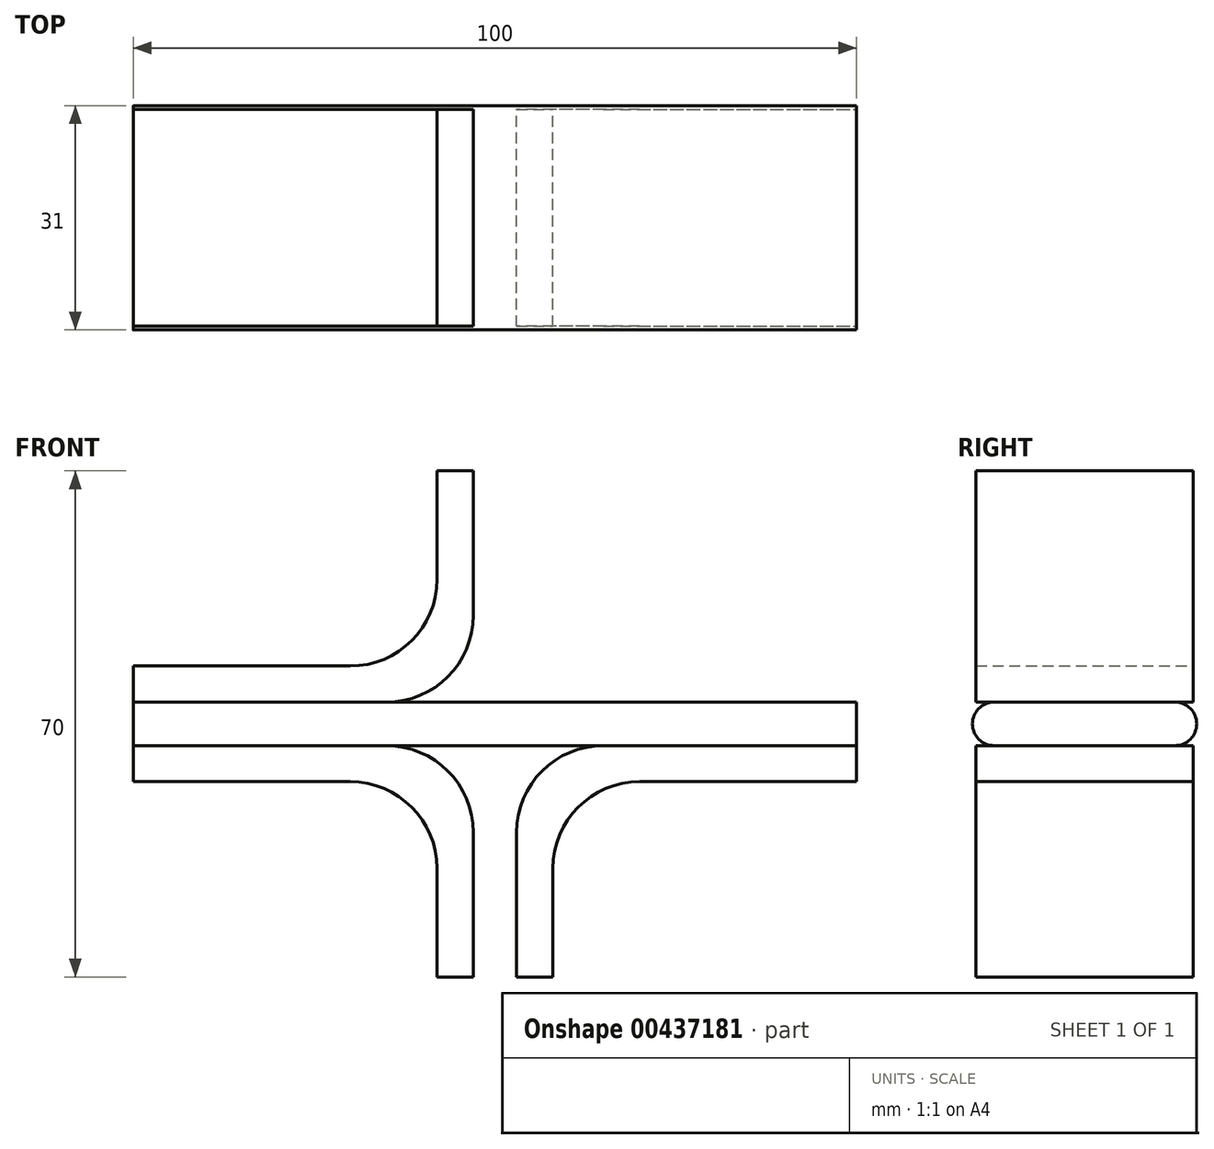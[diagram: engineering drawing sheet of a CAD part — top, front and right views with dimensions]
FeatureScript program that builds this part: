
annotation { "Feature Type Name" : "Feature", "Feature Type Description" : "" }
export const myFeature = defineFeature(function(context is Context, id is Id, definition is map)
    precondition{}
    {
        {
            var Q0;
            Q0=qCreatedBy(makeId("Right.planeOp"),FACE);
            var sketch = newSketch(context, id + "F0", { "sketchPlane" : qUnion([Q0])});
            skArc(sketch, "E0", {"start": v(-12.5, 3) * mm, "mid": v(-15.5, 0) * mm, "end": v(-12.5, -3) * mm});
            skArc(sketch, "E1", {"start": v(12.5, 3) * mm, "mid": v(15.5, 0) * mm, "end": v(12.5, -3) * mm});
            skLineSegment(sketch, "E2", {"start": v(-12.5, 3) * mm, "end": v(12.5, 3) * mm});
            skLineSegment(sketch, "E3", {"start": v(-12.5, -3) * mm, "end": v(12.5, -3) * mm});
            skSolve(sketch);
        }
        {
            var Q0;
            Q0=makeQuery(id+"F0.imprint","IMPRINT",FACE,{"disambiguationData":[TD([[makeQuery(id+"F0.imprint","IMPRINT",EDGE,{"derivedFrom":sQuery(id+"F0.wireOp",EDGE,"E0")}),1.0]])]});
            extrude(context, id + "F1", {"entities" : qUnion([Q0]), "endBound" : BoundingType.SYMMETRIC, "depth" : 100 * mm});
        }
        {
            var Q0;
            Q0=qCreatedBy(makeId("Front.planeOp"),FACE);
            var sketch = newSketch(context, id + "F2", { "sketchPlane" : qUnion([Q0])});
            skLineSegment(sketch, "E4", {"start": v(-50, 8) * mm, "end": v(-50, 3) * mm});
            skLineSegment(sketch, "E5", {"start": v(-50, 3) * mm, "end": v(-15, 3) * mm});
            skLineSegment(sketch, "E6", {"start": v(-3, 15) * mm, "end": v(-3, 35) * mm});
            skLineSegment(sketch, "E7", {"start": v(-3, 35) * mm, "end": v(-8, 35) * mm});
            skLineSegment(sketch, "E8", {"start": v(-8, 35) * mm, "end": v(-8, 20) * mm});
            skLineSegment(sketch, "E9", {"start": v(-20, 8) * mm, "end": v(-50, 8) * mm});
            skPoint(sketch, "E10.visualSharp", {"position": v(-3, 3) * mm});
            skArc(sketch, "E10.filletArc", {"start": v(-15, 3) * mm, "mid": v(-6.51, 6.51) * mm, "end": v(-3, 15) * mm});
            skPoint(sketch, "E11.visualSharp", {"position": v(-8, 8) * mm});
            skArc(sketch, "E11.filletArc", {"start": v(-20, 8) * mm, "mid": v(-11.51, 11.51) * mm, "end": v(-8, 20) * mm});
            skLineSegment(sketch, "E12.0.0", {"start": v(-50, 3) * mm, "end": v(-50, -3) * mm});
            skLineSegment(sketch, "E12.0.1", {"start": v(-50, -3) * mm, "end": v(50, -3) * mm});
            skLineSegment(sketch, "E12.0.2", {"start": v(50, -3) * mm, "end": v(50, 3) * mm});
            skLineSegment(sketch, "E12.0.3", {"start": v(50, 3) * mm, "end": v(-50, 3) * mm});
            skLineSegment(sketch, "E13.MirrorCS", {"start": v(-20, -8) * mm, "end": v(-50, -8) * mm});
            skLineSegment(sketch, "E14.MirrorCS", {"start": v(-50, -8) * mm, "end": v(-50, -3) * mm});
            skLineSegment(sketch, "E15.MirrorCS", {"start": v(-50, -3) * mm, "end": v(-15, -3) * mm});
            skArc(sketch, "E16.MirrorCS", {"start": v(-15, -3) * mm, "mid": v(-6.51, -6.51) * mm, "end": v(-3, -15) * mm});
            skArc(sketch, "E17.MirrorCS", {"start": v(-20, -8) * mm, "mid": v(-11.51, -11.51) * mm, "end": v(-8, -20) * mm});
            skLineSegment(sketch, "E18.MirrorCS", {"start": v(-8, -35) * mm, "end": v(-8, -20) * mm});
            skLineSegment(sketch, "E19.MirrorCS", {"start": v(-3, -35) * mm, "end": v(-8, -35) * mm});
            skLineSegment(sketch, "E20.MirrorCS", {"start": v(-3, -15) * mm, "end": v(-3, -35) * mm});
            skArc(sketch, "E21.MirrorCS", {"start": v(15, 3) * mm, "mid": v(6.51, 6.51) * mm, "end": v(3, 15) * mm});
            skLineSegment(sketch, "E22.MirrorCS", {"start": v(50, 3) * mm, "end": v(15, 3) * mm});
            skLineSegment(sketch, "E23.MirrorCS", {"start": v(20, 8) * mm, "end": v(50, 8) * mm});
            skArc(sketch, "E24.MirrorCS", {"start": v(20, 8) * mm, "mid": v(11.51, 11.51) * mm, "end": v(8, 20) * mm});
            skLineSegment(sketch, "E25.MirrorCS", {"start": v(8, 35) * mm, "end": v(8, 20) * mm});
            skLineSegment(sketch, "E26.MirrorCS", {"start": v(3, 15) * mm, "end": v(3, 35) * mm});
            skLineSegment(sketch, "E27.MirrorCS", {"start": v(3, 35) * mm, "end": v(8, 35) * mm});
            skLineSegment(sketch, "E28.MirrorCS", {"start": v(50, 8) * mm, "end": v(50, 3) * mm});
            skLineSegment(sketch, "E29.MirrorCS", {"start": v(3, -35) * mm, "end": v(8, -35) * mm});
            skLineSegment(sketch, "E30.MirrorCS", {"start": v(8, -35) * mm, "end": v(8, -20) * mm});
            skLineSegment(sketch, "E31.MirrorCS", {"start": v(3, -15) * mm, "end": v(3, -35) * mm});
            skArc(sketch, "E32.MirrorCS", {"start": v(15, -3) * mm, "mid": v(6.51, -6.51) * mm, "end": v(3, -15) * mm});
            skLineSegment(sketch, "E33.MirrorCS", {"start": v(20, -8) * mm, "end": v(50, -8) * mm});
            skLineSegment(sketch, "E34.MirrorCS", {"start": v(50, -8) * mm, "end": v(50, -3) * mm});
            skArc(sketch, "E35.MirrorCS", {"start": v(20, -8) * mm, "mid": v(11.51, -11.51) * mm, "end": v(8, -20) * mm});
            skLineSegment(sketch, "E36.MirrorCS", {"start": v(50, -3) * mm, "end": v(-50, -3) * mm, "construction": true});
            skSolve(sketch);
        }
        {
            var Q0;
            {var subQ1=sQuery(id+"F2.wireOp",EDGE,"E4");Q0=makeQuery(id+"F2.imprint","IMPRINT",FACE,{"disambiguationData":[TD([[makeQuery(id+"F2.imprint","IMPRINT",EDGE,{"derivedFrom":subQ1}),1.0]])]});}
            var Q1;
            Q1=makeQuery(id+"F2.imprint","IMPRINT",FACE,{"disambiguationData":[TD([[makeQuery(id+"F2.imprint","IMPRINT",EDGE,{"derivedFrom":sQuery(id+"F2.wireOp",EDGE,"E21.MirrorCS")}),-1.0]])]});
            var Q2;
            Q2=makeQuery(id+"F2.imprint","IMPRINT",FACE,{"disambiguationData":[TD([[makeQuery(id+"F2.imprint","IMPRINT",EDGE,{"derivedFrom":sQuery(id+"F2.wireOp",EDGE,"E13.MirrorCS")}),-1.0]])]});
            var Q3;
            Q3=makeQuery(id+"F2.imprint","IMPRINT",FACE,{"disambiguationData":[TD([[makeQuery(id+"F2.imprint","IMPRINT",EDGE,{"derivedFrom":sQuery(id+"F2.wireOp",EDGE,"E29.MirrorCS")}),1.0]])]});
            extrude(context, id + "F3", {"entities" : qUnion([Q0, Q1, Q2, Q3]), "endBound" : BoundingType.SYMMETRIC, "depth" : 30 * mm});
        }
    });
